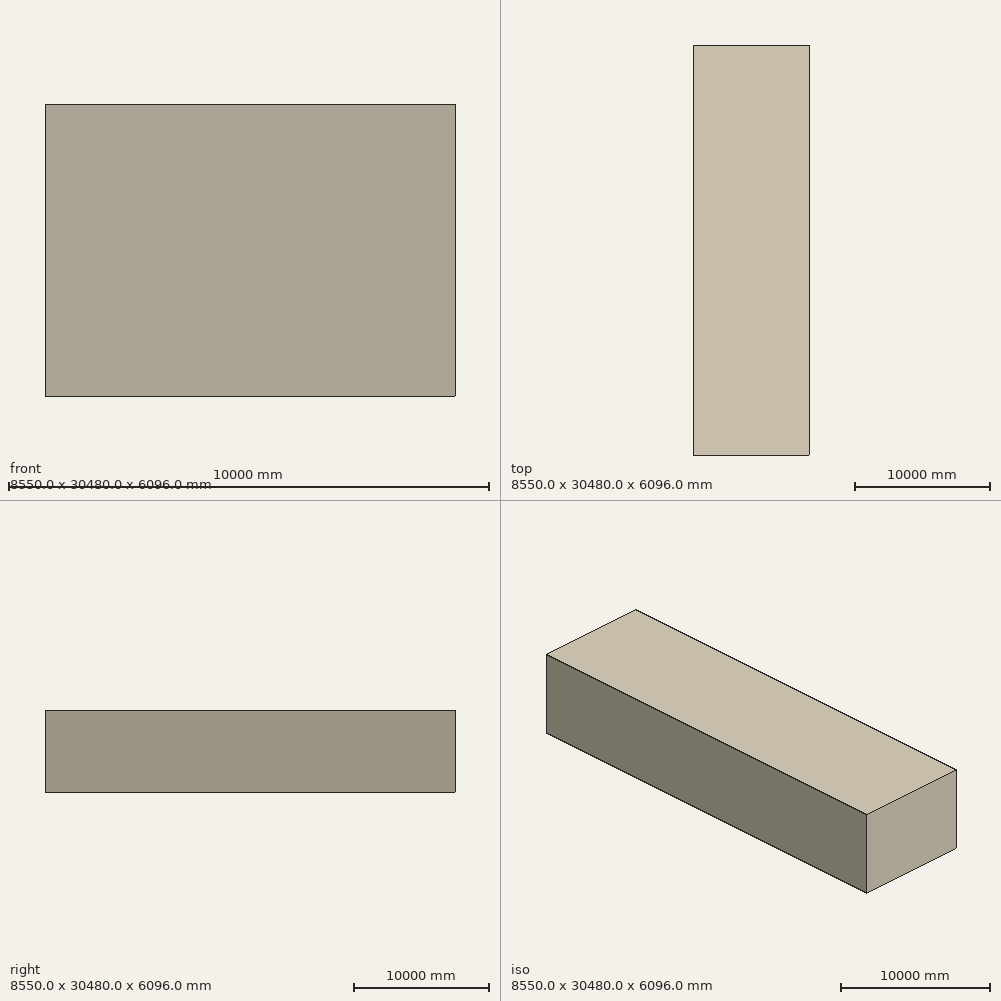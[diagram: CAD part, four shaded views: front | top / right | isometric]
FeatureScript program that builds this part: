
annotation { "Feature Type Name" : "Feature", "Feature Type Description" : "" }
export const myFeature = defineFeature(function(context is Context, id is Id, definition is map)
    precondition{}
    {
        {
            var Q0;
            Q0=qCreatedBy(makeId("Front.planeOp"),FACE);
            var sketch = newSketch(context, id + "F0", { "sketchPlane" : qUnion([Q0])});
            skLineSegment(sketch, "E0.bottom", {"start": v(-4274.76, 3120.8) * mm, "end": v(4275.24, 3120.8) * mm});
            skLineSegment(sketch, "E0.top", {"start": v(-4274.76, -2975.2) * mm, "end": v(4275.24, -2975.2) * mm});
            skLineSegment(sketch, "E0.left", {"start": v(-4274.76, 3120.8) * mm, "end": v(-4274.76, -2975.2) * mm});
            skLineSegment(sketch, "E0.right", {"start": v(4275.24, 3120.8) * mm, "end": v(4275.24, -2975.2) * mm});
            skSolve(sketch);
        }
        {
            var Q0;
            Q0=makeQuery(id+"F0.imprint","IMPRINT",FACE,{"disambiguationData":[TD([[makeQuery(id+"F0.imprint","IMPRINT",EDGE,{"derivedFrom":sQuery(id+"F0.wireOp",EDGE,"E0.bottom")}),-1.0]])]});
            extrude(context, id + "F1", {"entities" : qUnion([Q0]), "depth" : 30480 * mm});
        }
    });
